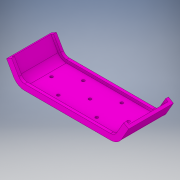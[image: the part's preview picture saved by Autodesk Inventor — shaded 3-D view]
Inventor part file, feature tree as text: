
AUTODESK INVENTOR PART (.ipt)
format: ipt  version: 2019 (Build 230136000, 136)  size: 200,704 bytes
history: native  units: mm
features: sketch x5, extrude x3, hole x2, projected_geometry x2, plane x1, mirror x1
ambient origin geometry x8: Origin, YZ Plane, XZ Plane, XY Plane, X Axis, Y Axis, Z Axis, Center Point
bodies: Solid1 (feature_tree)
feature tree (14):
  extrude  "Extrusion1"  Depth=40.0mm
  hole  "Hole1"  [1 undecoded]
  hole  "Hole2"  [1 undecoded]
  plane  "Work Plane2"
  extrude  "Extrusion3"  Depth=3.0mm TaperAngle=0.0deg
  extrude  "Extrusion4"  Depth=3.0mm
  mirror  "Mirror2"
  sketch  "Sketch1"  dims[d1=40.0mm d2=0.0mm d3=40.0mm]
  sketch  "Sketch2"  dims[d4=40.0mm]
  sketch  "Sketch3"  dims[d5=3.0mm d6=6.0mm d7=11.5mm d8=2.0mm d9=90.0deg d10=8.0mm d11=20.594885mm d12=20.0mm]
  sketch  "Sketch5"  dims[d13=20.0mm d14=7.0mm]
  projected_geometry  "Projected Loop2"
  sketch  "Sketch6"  dims[d15=3.0mm d16=6.0mm d17=4.0mm d18=2.0mm d19=90.0deg d20=8.0mm d21=20.594885mm d25=0.25mm d26=0.0mm d27=3.0mm d28=3.0mm d29=0.0mm]
  projected_geometry  "Projected Loop4"
note: 2 required parameter values undecoded (feature->parameter linkage not recoverable at this tier; creation-order binding heuristic only, values carry confidence <= 0.55)
